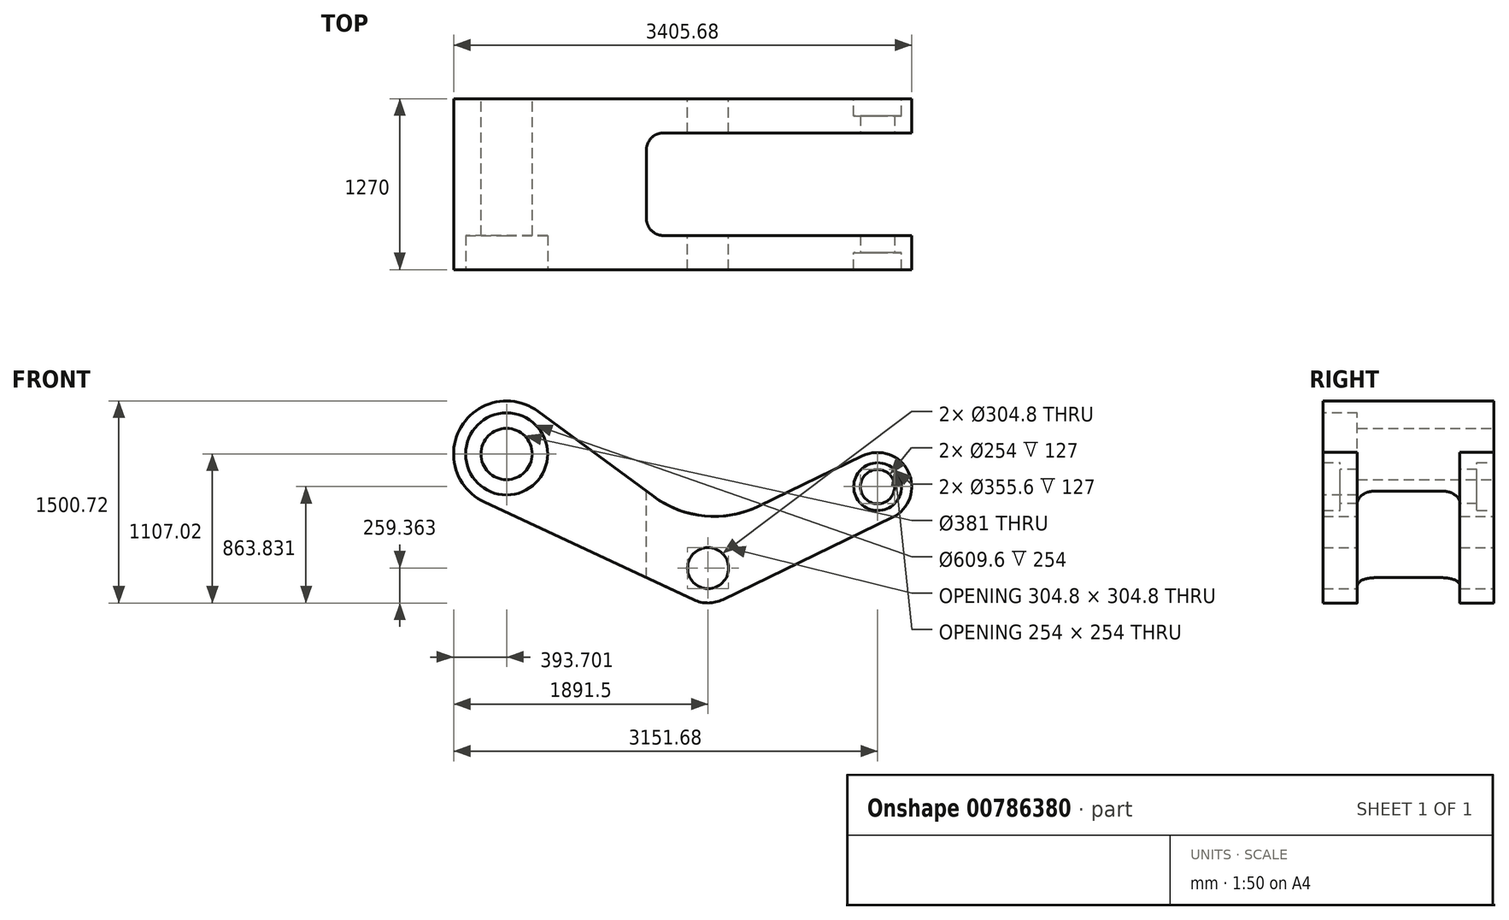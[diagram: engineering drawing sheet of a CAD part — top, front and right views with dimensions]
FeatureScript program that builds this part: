
annotation { "Feature Type Name" : "Feature", "Feature Type Description" : "" }
export const myFeature = defineFeature(function(context is Context, id is Id, definition is map)
    precondition{}
    {
        {
            var Q0;
            Q0=qCreatedBy(makeId("Front.planeOp"),FACE);
            var sketch = newSketch(context, id + "F0", { "sketchPlane" : qUnion([Q0])});
            skCircle(sketch, "E0", {"center": v(0, -1.79) * mm, "radius": 254 * mm});
            skCircle(sketch, "E1", {"center": v(0, 3.57) * mm, "radius": 152.4 * mm});
            skCircle(sketch, "E2", {"center": v(-1497.8, 851.23) * mm, "radius": 393.7 * mm});
            skCircle(sketch, "E3", {"center": v(-1497.8, 851.23) * mm, "radius": 190.5 * mm});
            skCircle(sketch, "E4", {"center": v(1260.18, 608.04) * mm, "radius": 254 * mm});
            skCircle(sketch, "E5", {"center": v(1260.18, 608.04) * mm, "radius": 177.8 * mm});
            skLineSegment(sketch, "E6", {"start": v(-1264.33, 1168.23) * mm, "end": v(-405.57, 535.77) * mm});
            skLineSegment(sketch, "E7", {"start": v(378.23, 463.42) * mm, "end": v(1149.53, 836.68) * mm});
            skLineSegment(sketch, "E8", {"start": v(1370.82, 379.4) * mm, "end": v(110.64, -230.42) * mm});
            skLineSegment(sketch, "E9", {"start": v(-1664.27, 494.45) * mm, "end": v(-107.4, -231.96) * mm});
            skArc(sketch, "E10.filletArc", {"start": v(-38.58, 265.49) * mm, "mid": v(-35.4, 264.28) * mm, "end": v(-32.05, 264.88) * mm});
            skArc(sketch, "E11.filletArc", {"start": v(-405.57, 535.77) * mm, "mid": v(-23.74, 390.56) * mm, "end": v(378.23, 463.42) * mm});
            skSolve(sketch);
        }
        {
            var Q0;
            Q0=makeQuery(id+"F0.imprint","IMPRINT",FACE,{"disambiguationData":[TD([[makeQuery(id+"F0.imprint","IMPRINT",EDGE,{"derivedFrom":sQuery(id+"F0.wireOp",EDGE,"E3")}),-1.0]])]});
            var Q1;
            {var subQ0=sQuery(id+"F0.wireOp",EDGE,"E6");Q1=makeQuery(id+"F0.imprint","IMPRINT",FACE,{"disambiguationData":[TD([[makeQuery(id+"F0.imprint","IMPRINT",EDGE,{"derivedFrom":subQ0}),-1.0]])]});}
            var Q2;
            Q2=makeQuery(id+"F0.imprint","IMPRINT",FACE,{"disambiguationData":[TD([[makeQuery(id+"F0.imprint","IMPRINT",EDGE,{"derivedFrom":sQuery(id+"F0.wireOp",EDGE,"E1")}),-1.0]])]});
            var Q3;
            Q3=makeQuery(id+"F0.imprint","IMPRINT",FACE,{"disambiguationData":[TD([[makeQuery(id+"F0.imprint","IMPRINT",EDGE,{"derivedFrom":sQuery(id+"F0.wireOp",EDGE,"E5")}),-1.0]])]});
            extrude(context, id + "F1", {"entities" : qUnion([Q0, Q1, Q2, Q3]), "endBound" : BoundingType.SYMMETRIC, "depth" : 1270 * mm, "offsetDistance" : 25.4 * mm});
        }
        {
            var Q0;
            Q0=makeQuery(id+"F0.imprint","IMPRINT",FACE,{"disambiguationData":[TD([[makeQuery(id+"F0.imprint","IMPRINT",EDGE,{"derivedFrom":sQuery(id+"F0.wireOp",EDGE,"E5")}),1.0]])]});
            extrude(context, id + "F2", {"entities" : qUnion([Q0]), "operationType" : NewBodyOperationType.ADD, "endBound" : BoundingType.SYMMETRIC, "depth" : 1016 * mm, "offsetDistance" : 25.4 * mm});
        }
        {
            var Q0;
            Q0=makeQuery(id+"F1.opExtrude","CAP_FACE",FACE,{"disambiguationData":[OSD([sQuery(id+"F0.wireOp",EDGE,"E0"),sQuery(id+"F0.wireOp",EDGE,"E1"),sQuery(id+"F0.wireOp",EDGE,"E2"),sQuery(id+"F0.wireOp",EDGE,"E3"),sQuery(id+"F0.wireOp",EDGE,"E4"),sQuery(id+"F0.wireOp",EDGE,"E5"),sQuery(id+"F0.wireOp",EDGE,"E6"),sQuery(id+"F0.wireOp",EDGE,"E7"),sQuery(id+"F0.wireOp",EDGE,"E8"),sQuery(id+"F0.wireOp",EDGE,"E9"),sQuery(id+"F0.wireOp",EDGE,"E11.filletArc")])],"isStart":false});
            var sketch = newSketch(context, id + "F3", { "sketchPlane" : qUnion([Q0])});
            skCircle(sketch, "E12", {"center": v(-1497.8, 851.23) * mm, "radius": 304.8 * mm});
            skCircle(sketch, "E13", {"center": v(1260.18, 608.04) * mm, "radius": 127 * mm});
            skSolve(sketch);
        }
        {
            var Q0;
            Q0=makeQuery(id+"F3.imprint","IMPRINT",FACE,{"disambiguationData":[TD([[makeQuery(id+"F3.imprint","IMPRINT",EDGE,{"derivedFrom":sQuery(id+"F3.wireOp",EDGE,"E13")}),1.0]])]});
            var Q1;
            Q1=sQuery(id+"F3.wireOp",EDGE,"E13");
            extrude(context, id + "F4", {"entities" : qUnion([Q0]), "operationType" : NewBodyOperationType.REMOVE, "surfaceEntities" : qUnion([Q1]), "endBound" : BoundingType.THROUGH_ALL, "oppositeDirection" : true, "depth" : 762 * mm, "offsetDistance" : 25.4 * mm});
        }
        {
            var Q0;
            Q0=makeQuery(id+"F3.imprint","IMPRINT",FACE,{"disambiguationData":[TD([[makeQuery(id+"F3.imprint","IMPRINT",EDGE,{"derivedFrom":sQuery(id+"F3.wireOp",EDGE,"E12")}),1.0]])]});
            var Q1;
            Q1=sQuery(id+"F3.wireOp",EDGE,"E12");
            extrude(context, id + "F5", {"entities" : qUnion([Q0]), "operationType" : NewBodyOperationType.REMOVE, "surfaceEntities" : qUnion([Q1]), "oppositeDirection" : true, "depth" : 254 * mm, "offsetDistance" : 25.4 * mm});
        }
        {
            var Q0;
            Q0=qCreatedBy(makeId("Top.planeOp"),FACE);
            var sketch = newSketch(context, id + "F6", { "sketchPlane" : qUnion([Q0])});
            skLineSegment(sketch, "E14.bottom", {"start": v(1827.33, 381) * mm, "end": v(-458.67, 381) * mm});
            skLineSegment(sketch, "E14.top", {"start": v(1827.33, -381) * mm, "end": v(-458.67, -381) * mm});
            skLineSegment(sketch, "E14.left", {"start": v(1827.33, 381) * mm, "end": v(1827.33, -381) * mm});
            skLineSegment(sketch, "E14.right", {"start": v(-458.67, 381) * mm, "end": v(-458.67, -381) * mm});
            skPoint(sketch, "E14.middle", {"position": v(684.33, 0) * mm});
            skSolve(sketch);
        }
        {
            var Q0;
            Q0=makeQuery(id+"F6.imprint","IMPRINT",FACE,{"disambiguationData":[TD([[makeQuery(id+"F6.imprint","IMPRINT",EDGE,{"derivedFrom":sQuery(id+"F6.wireOp",EDGE,"E14.bottom")}),1.0]])]});
            extrude(context, id + "F7", {"entities" : qUnion([Q0]), "operationType" : NewBodyOperationType.REMOVE, "endBound" : BoundingType.SYMMETRIC, "oppositeDirection" : true, "depth" : 2540 * mm, "offsetDistance" : 25.4 * mm});
        }
        {
            var Q0;
            Q0=makeQuery(id+"F7.boolean.opBoolean","COPY",EDGE,{"derivedFrom":makeQuery(id+"F7.opExtrude","SWEPT_EDGE",EDGE,{"disambiguationData":[OSD([sQuery(id+"F6.wireOp",EDGE,"E14.bottom"),sQuery(id+"F6.wireOp",EDGE,"E14.right")])]})});
            var Q1;
            Q1=makeQuery(id+"F7.boolean.opBoolean","COPY",EDGE,{"derivedFrom":makeQuery(id+"F7.opExtrude","SWEPT_EDGE",EDGE,{"disambiguationData":[OSD([sQuery(id+"F6.wireOp",EDGE,"E14.top"),sQuery(id+"F6.wireOp",EDGE,"E14.right")])]})});
            fillet(context, id + "F8", {"entities" : qUnion([Q0, Q1]), "radius" : 127 * mm, "tangentPropagation" : true, "allowEdgeOverflow" : false});
        }
    });
